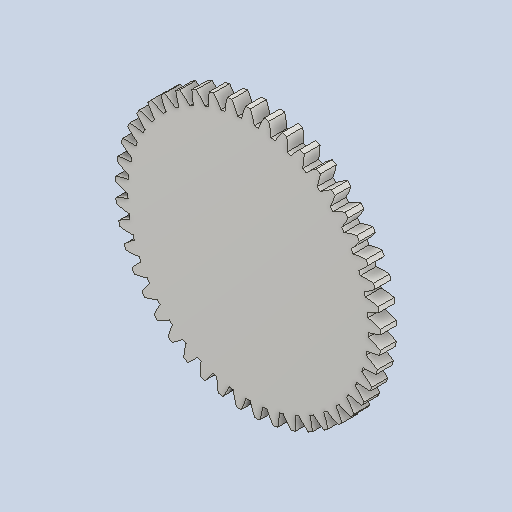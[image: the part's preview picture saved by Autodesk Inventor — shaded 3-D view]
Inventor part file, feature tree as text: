
AUTODESK INVENTOR PART (.ipt)
format: ipt  version: 2024 (Build 280153000, 153)  size: 316,928 bytes
history: native  units: mm (DEFAULTED — no unit token found)
features: plane x3, other x3, extrude x1, sketch x1
ambient origin geometry x8: Origin, YZ Plane, XZ Plane, XY Plane, X Axis, Y Axis, Z Axis, Center Point
bodies: Solid1 (feature_tree)
feature tree (8):
  extrude  "Extrusion1"  Depth=20.0mm TaperAngle=0.0deg
  plane  "Work Plane2"
  plane  "Work Plane8"
  plane  "Work Plane9"
  other  "Spur Gear"
  sketch  "Sketch1"  dims[d0=333.0mm d1=20.0mm d2=0.0mm d3=315.0mm d4=10.0mm d5=0.0mm d16=240.0mm d17=0.0mm d34=0.698132mm d39=0.0mm d41=0.0mm d43=240.0mm d46=240.0mm d47=0.0mm d48=0.0mm]
  other  "Srf1"
  other  "Pitch Diameter"
